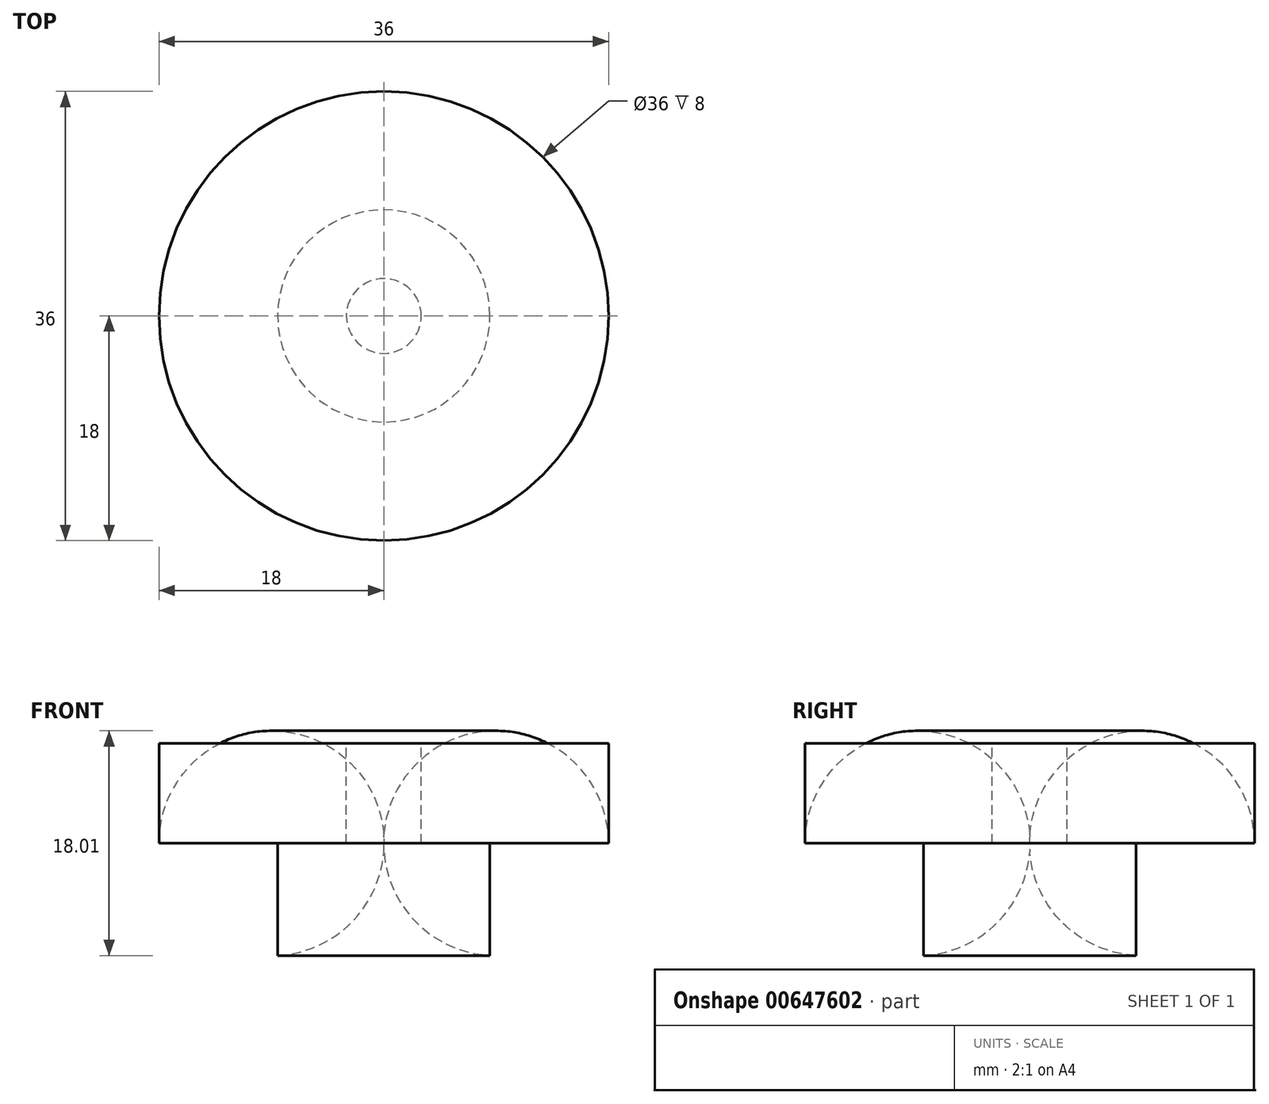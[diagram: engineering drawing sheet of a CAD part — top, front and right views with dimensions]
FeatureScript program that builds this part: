
annotation { "Feature Type Name" : "Feature", "Feature Type Description" : "" }
export const myFeature = defineFeature(function(context is Context, id is Id, definition is map)
    precondition{}
    {
        {
            var Q0;
            Q0=qCreatedBy(makeId("Front.planeOp"),FACE);
            var sketch = newSketch(context, id + "F0", { "sketchPlane" : qUnion([Q0])});
            skLineSegment(sketch, "E0", {"start": v(0, 17) * mm, "end": v(0, 0) * mm, "construction": true});
            skLineSegment(sketch, "E1", {"start": v(0, 17) * mm, "end": v(18, 17) * mm});
            skLineSegment(sketch, "E2", {"start": v(18, 17) * mm, "end": v(18, 9) * mm});
            skLineSegment(sketch, "E3", {"start": v(0, 0) * mm, "end": v(8.5, 0) * mm});
            skLineSegment(sketch, "E4", {"start": v(3, 17) * mm, "end": v(3, 9) * mm});
            skLineSegment(sketch, "E5", {"start": v(3, 9) * mm, "end": v(8.5, 9) * mm});
            skLineSegment(sketch, "E6", {"start": v(8.5, 9) * mm, "end": v(8.5, 0) * mm});
            skArc(sketch, "E7", {"start": v(8.5, 0) * mm, "mid": v(15.19, 2.46) * mm, "end": v(18, 9) * mm});
            skSolve(sketch);
        }
        {
            var Q0;
            {var subQ1=sQuery(id+"F0.wireOp",EDGE,"E2");Q0=makeQuery(id+"F0.imprint","IMPRINT",FACE,{"disambiguationData":[TD([[makeQuery(id+"F0.imprint","IMPRINT",EDGE,{"derivedFrom":subQ1}),-1.0]])]});}
            var Q1;
            Q1=sQuery(id+"F0.wireOp",EDGE,"E0");
            revolve(context, id + "F1", {"entities" : qUnion([Q0]), "axis" : qUnion([Q1]), "revolveType" : RevolveType.FULL});
        }
    });
